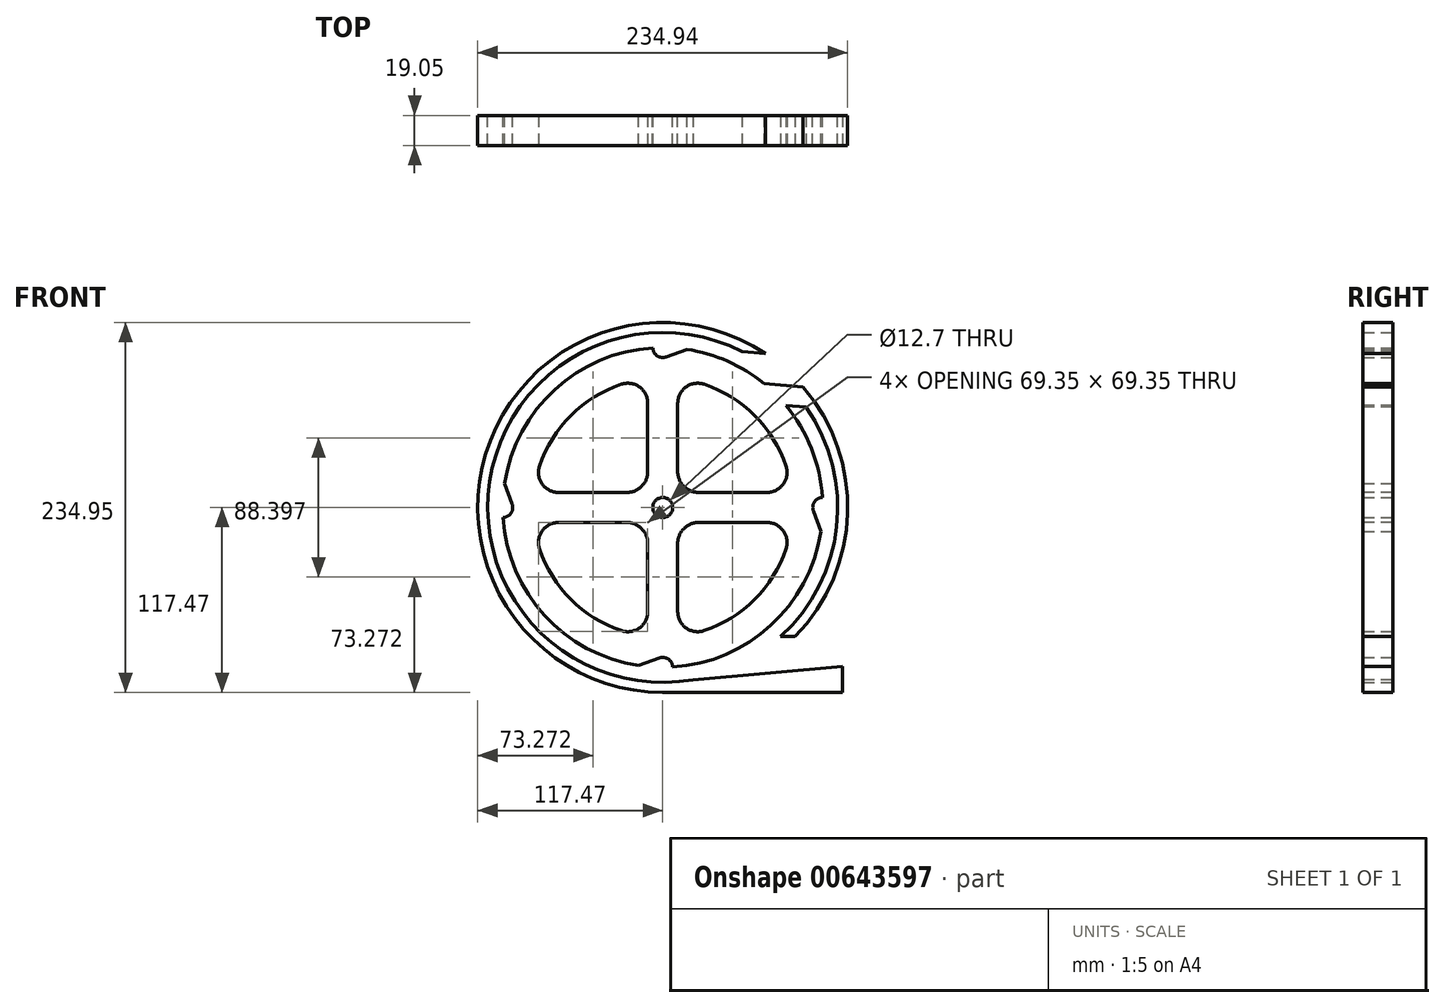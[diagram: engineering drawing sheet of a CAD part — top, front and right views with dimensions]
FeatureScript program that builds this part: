
annotation { "Feature Type Name" : "Feature", "Feature Type Description" : "" }
export const myFeature = defineFeature(function(context is Context, id is Id, definition is map)
    precondition{}
    {
        {
            var Q0;
            Q0=qCreatedBy(makeId("Front.planeOp"),FACE);
            var sketch = newSketch(context, id + "F0", { "sketchPlane" : qUnion([Q0])});
            skArc(sketch, "E0", {"start": v(-6.35, 101.4) * mm, "mid": v(-68.57, 74.97) * mm, "end": v(-100.43, 15.36) * mm});
            skArc(sketch, "E1", {"start": v(-6.35, 101.4) * mm, "mid": v(-3.56, 96.34) * mm, "end": v(2.17, 95.63) * mm});
            skLineSegment(sketch, "E2", {"start": v(0, 101.6) * mm, "end": v(18.57, 101.6) * mm, "construction": true});
            skLineSegment(sketch, "E3", {"start": v(15.36, 100.43) * mm, "end": v(2.17, 95.63) * mm});
            skLineSegment(sketch, "E4", {"start": v(15.36, 100.43) * mm, "end": v(18.57, 101.6) * mm, "construction": true});
            skLineSegment(sketch, "E5.1.0", {"start": v(-100.43, 15.36) * mm, "end": v(-95.63, 2.17) * mm});
            skArc(sketch, "E5.1.1", {"start": v(-101.4, -6.35) * mm, "mid": v(-96.34, -3.56) * mm, "end": v(-95.63, 2.17) * mm});
            skLineSegment(sketch, "E5.2.0", {"start": v(-15.36, -100.43) * mm, "end": v(-2.17, -95.63) * mm});
            skArc(sketch, "E5.2.1", {"start": v(6.35, -101.4) * mm, "mid": v(3.56, -96.34) * mm, "end": v(-2.17, -95.63) * mm});
            skLineSegment(sketch, "E5.3.0", {"start": v(100.43, -15.36) * mm, "end": v(95.63, -2.17) * mm});
            skArc(sketch, "E5.3.1", {"start": v(101.4, 6.35) * mm, "mid": v(96.34, 3.56) * mm, "end": v(95.63, -2.17) * mm});
            skArc(sketch, "E6.trimOffspring", {"start": v(-101.4, -6.35) * mm, "mid": v(-74.97, -68.57) * mm, "end": v(-15.36, -100.43) * mm});
            skArc(sketch, "E7.trimOffspring", {"start": v(101.4, 6.35) * mm, "mid": v(74.97, 68.57) * mm, "end": v(15.36, 100.43) * mm});
            skArc(sketch, "E8.trimOffspring", {"start": v(6.35, -101.4) * mm, "mid": v(68.57, -74.97) * mm, "end": v(100.43, -15.36) * mm});
            skCircle(sketch, "E9", {"center": v(0, 0) * mm, "radius": 6.35 * mm});
            skSolve(sketch);
        }
        {
            var Q0;
            Q0=makeQuery(id+"F0.imprint","IMPRINT",FACE,{"disambiguationData":[TD([[makeQuery(id+"F0.imprint","IMPRINT",EDGE,{"derivedFrom":sQuery(id+"F0.wireOp",EDGE,"E0")}),1.0]])]});
            extrude(context, id + "F1", {"entities" : qUnion([Q0]), "depth" : 19.05 * mm, "offsetDistance" : 25.4 * mm});
        }
        {
            var Q0;
            Q0=makeQuery(id+"F1.opExtrude","CAP_FACE",FACE,{"disambiguationData":[OSD([sQuery(id+"F0.wireOp",EDGE,"E0"),sQuery(id+"F0.wireOp",EDGE,"E1"),sQuery(id+"F0.wireOp",EDGE,"E3"),sQuery(id+"F0.wireOp",EDGE,"E5.1.0"),sQuery(id+"F0.wireOp",EDGE,"E5.1.1"),sQuery(id+"F0.wireOp",EDGE,"E5.2.0"),sQuery(id+"F0.wireOp",EDGE,"E5.2.1"),sQuery(id+"F0.wireOp",EDGE,"E5.3.0"),sQuery(id+"F0.wireOp",EDGE,"E5.3.1"),sQuery(id+"F0.wireOp",EDGE,"E6.trimOffspring"),sQuery(id+"F0.wireOp",EDGE,"E7.trimOffspring"),sQuery(id+"F0.wireOp",EDGE,"E8.trimOffspring"),sQuery(id+"F0.wireOp",EDGE,"E9")])],"isStart":false});
            var sketch = newSketch(context, id + "F2", { "sketchPlane" : qUnion([Q0])});
            skCircle(sketch, "E10", {"center": v(0, 0) * mm, "radius": 19.05 * mm});
            skCircle(sketch, "E11", {"center": v(0, 0) * mm, "radius": 82.55 * mm});
            skLineSegment(sketch, "E12", {"start": v(9.53, 16.5) * mm, "end": v(9.53, 82) * mm});
            skLineSegment(sketch, "E13", {"start": v(-9.53, 16.5) * mm, "end": v(-9.53, 82) * mm});
            skLineSegment(sketch, "E14", {"start": v(0, 0) * mm, "end": v(0, 82.55) * mm, "construction": true});
            skLineSegment(sketch, "E15.1.0", {"start": v(-16.5, 9.53) * mm, "end": v(-82, 9.52) * mm});
            skLineSegment(sketch, "E15.1.1", {"start": v(-16.5, -9.52) * mm, "end": v(-82, -9.53) * mm});
            skLineSegment(sketch, "E15.2.0", {"start": v(-9.53, -16.5) * mm, "end": v(-9.52, -82) * mm});
            skLineSegment(sketch, "E15.2.1", {"start": v(9.52, -16.5) * mm, "end": v(9.53, -82) * mm});
            skLineSegment(sketch, "E15.3.0", {"start": v(16.5, -9.53) * mm, "end": v(82, -9.52) * mm});
            skLineSegment(sketch, "E15.3.1", {"start": v(16.5, 9.52) * mm, "end": v(82, 9.53) * mm});
            skSolve(sketch);
        }
        {
            var Q0;
            {var subQ0=sQuery(id+"F2.wireOp",EDGE,"E12");Q0=makeQuery(id+"F2.imprint","IMPRINT",FACE,{"disambiguationData":[TD([[makeQuery(id+"F2.imprint","IMPRINT",EDGE,{"derivedFrom":subQ0}),-1.0]])]});}
            var Q1;
            {var subQ0=sQuery(id+"F2.wireOp",EDGE,"E13");Q1=makeQuery(id+"F2.imprint","IMPRINT",FACE,{"disambiguationData":[TD([[makeQuery(id+"F2.imprint","IMPRINT",EDGE,{"derivedFrom":subQ0}),1.0]])]});}
            var Q2;
            {var subQ0=sQuery(id+"F2.wireOp",EDGE,"E15.1.1");Q2=makeQuery(id+"F2.imprint","IMPRINT",FACE,{"disambiguationData":[TD([[makeQuery(id+"F2.imprint","IMPRINT",EDGE,{"derivedFrom":subQ0}),1.0]])]});}
            var Q3;
            {var subQ0=sQuery(id+"F2.wireOp",EDGE,"E15.2.1");Q3=makeQuery(id+"F2.imprint","IMPRINT",FACE,{"disambiguationData":[TD([[makeQuery(id+"F2.imprint","IMPRINT",EDGE,{"derivedFrom":subQ0}),1.0]])]});}
            var Q4;
            {var subQ0=sQuery(id+"F2.wireOp",EDGE,"E15.3.1");Q4=makeQuery(id+"F2.imprint","IMPRINT",FACE,{"disambiguationData":[TD([[makeQuery(id+"F2.imprint","IMPRINT",EDGE,{"derivedFrom":subQ0}),1.0]])]});}
            extrude(context, id + "F3", {"entities" : qUnion([Q0, Q1, Q2, Q3, Q4]), "operationType" : NewBodyOperationType.REMOVE, "oppositeDirection" : true, "depth" : 19.05 * mm, "offsetDistance" : 25.4 * mm});
        }
        {
            var Q0;
            Q0=makeQuery(id+"F3.boolean.opBoolean","COPY",EDGE,{"derivedFrom":makeQuery(id+"F3.opExtrude","SWEPT_EDGE",EDGE,{"disambiguationData":[OSD([sQuery(id+"F2.wireOp",EDGE,"E11"),sQuery(id+"F2.wireOp",EDGE,"E13")])]})});
            var Q1;
            Q1=makeQuery(id+"F3.boolean.opBoolean","COPY",EDGE,{"derivedFrom":makeQuery(id+"F3.opExtrude","SWEPT_EDGE",EDGE,{"disambiguationData":[OSD([sQuery(id+"F2.wireOp",EDGE,"E11"),sQuery(id+"F2.wireOp",EDGE,"E15.1.0")])]})});
            var Q2;
            Q2=makeQuery(id+"F3.boolean.opBoolean","COPY",EDGE,{"derivedFrom":makeQuery(id+"F3.opExtrude","SWEPT_EDGE",EDGE,{"disambiguationData":[OSD([sQuery(id+"F2.wireOp",EDGE,"E10"),sQuery(id+"F2.wireOp",EDGE,"E13")])]})});
            var Q3;
            Q3=makeQuery(id+"F3.boolean.opBoolean","COPY",EDGE,{"derivedFrom":makeQuery(id+"F3.opExtrude","SWEPT_EDGE",EDGE,{"disambiguationData":[OSD([sQuery(id+"F2.wireOp",EDGE,"E10"),sQuery(id+"F2.wireOp",EDGE,"E15.1.0")])]})});
            var Q4;
            Q4=makeQuery(id+"F3.boolean.opBoolean","COPY",EDGE,{"derivedFrom":makeQuery(id+"F3.opExtrude","SWEPT_EDGE",EDGE,{"disambiguationData":[OSD([sQuery(id+"F2.wireOp",EDGE,"E11"),sQuery(id+"F2.wireOp",EDGE,"c7ea23de-dd5f-4fa7-8742-d0bc3a6b1323.3.4.0")])]})});
            var Q5;
            Q5=makeQuery(id+"F3.boolean.opBoolean","COPY",EDGE,{"derivedFrom":makeQuery(id+"F3.opExtrude","SWEPT_EDGE",EDGE,{"disambiguationData":[OSD([sQuery(id+"F2.wireOp",EDGE,"E11"),sQuery(id+"F2.wireOp",EDGE,"E12")])]})});
            var Q6;
            Q6=makeQuery(id+"F3.boolean.opBoolean","COPY",EDGE,{"derivedFrom":makeQuery(id+"F3.opExtrude","SWEPT_EDGE",EDGE,{"disambiguationData":[OSD([sQuery(id+"F2.wireOp",EDGE,"E10"),sQuery(id+"F2.wireOp",EDGE,"E12")])]})});
            var Q7;
            Q7=makeQuery(id+"F3.boolean.opBoolean","COPY",EDGE,{"derivedFrom":makeQuery(id+"F3.opExtrude","SWEPT_EDGE",EDGE,{"disambiguationData":[OSD([sQuery(id+"F2.wireOp",EDGE,"E10"),sQuery(id+"F2.wireOp",EDGE,"c7ea23de-dd5f-4fa7-8742-d0bc3a6b1323.3.4.0")])]})});
            var Q8;
            Q8=makeQuery(id+"F3.boolean.opBoolean","COPY",EDGE,{"derivedFrom":makeQuery(id+"F3.opExtrude","SWEPT_EDGE",EDGE,{"disambiguationData":[OSD([sQuery(id+"F2.wireOp",EDGE,"E10"),sQuery(id+"F2.wireOp",EDGE,"E15.3.1")])]})});
            var Q9;
            Q9=makeQuery(id+"F3.boolean.opBoolean","COPY",EDGE,{"derivedFrom":makeQuery(id+"F3.opExtrude","SWEPT_EDGE",EDGE,{"disambiguationData":[OSD([sQuery(id+"F2.wireOp",EDGE,"E11"),sQuery(id+"F2.wireOp",EDGE,"E15.3.1")])]})});
            var Q10;
            Q10=makeQuery(id+"F3.boolean.opBoolean","COPY",EDGE,{"derivedFrom":makeQuery(id+"F3.opExtrude","SWEPT_EDGE",EDGE,{"disambiguationData":[OSD([sQuery(id+"F2.wireOp",EDGE,"E11"),sQuery(id+"F2.wireOp",EDGE,"c7ea23de-dd5f-4fa7-8742-d0bc3a6b1323.1.4.0")])]})});
            var Q11;
            Q11=makeQuery(id+"F3.boolean.opBoolean","COPY",EDGE,{"derivedFrom":makeQuery(id+"F3.opExtrude","SWEPT_EDGE",EDGE,{"disambiguationData":[OSD([sQuery(id+"F2.wireOp",EDGE,"E10"),sQuery(id+"F2.wireOp",EDGE,"c7ea23de-dd5f-4fa7-8742-d0bc3a6b1323.1.4.0")])]})});
            var Q12;
            Q12=makeQuery(id+"F3.boolean.opBoolean","COPY",EDGE,{"derivedFrom":makeQuery(id+"F3.opExtrude","SWEPT_EDGE",EDGE,{"disambiguationData":[OSD([sQuery(id+"F2.wireOp",EDGE,"E10"),sQuery(id+"F2.wireOp",EDGE,"E15.3.0")])]})});
            var Q13;
            Q13=makeQuery(id+"F3.boolean.opBoolean","COPY",EDGE,{"derivedFrom":makeQuery(id+"F3.opExtrude","SWEPT_EDGE",EDGE,{"disambiguationData":[OSD([sQuery(id+"F2.wireOp",EDGE,"E11"),sQuery(id+"F2.wireOp",EDGE,"E15.3.0")])]})});
            var Q14;
            Q14=makeQuery(id+"F3.boolean.opBoolean","COPY",EDGE,{"derivedFrom":makeQuery(id+"F3.opExtrude","SWEPT_EDGE",EDGE,{"disambiguationData":[OSD([sQuery(id+"F2.wireOp",EDGE,"E11"),sQuery(id+"F2.wireOp",EDGE,"E15.2.1")])]})});
            var Q15;
            Q15=makeQuery(id+"F3.boolean.opBoolean","COPY",EDGE,{"derivedFrom":makeQuery(id+"F3.opExtrude","SWEPT_EDGE",EDGE,{"disambiguationData":[OSD([sQuery(id+"F2.wireOp",EDGE,"E10"),sQuery(id+"F2.wireOp",EDGE,"E15.2.1")])]})});
            var Q16;
            Q16=makeQuery(id+"F3.boolean.opBoolean","COPY",EDGE,{"derivedFrom":makeQuery(id+"F3.opExtrude","SWEPT_EDGE",EDGE,{"disambiguationData":[OSD([sQuery(id+"F2.wireOp",EDGE,"E10"),sQuery(id+"F2.wireOp",EDGE,"E15.2.0")])]})});
            var Q17;
            Q17=makeQuery(id+"F3.boolean.opBoolean","COPY",EDGE,{"derivedFrom":makeQuery(id+"F3.opExtrude","SWEPT_EDGE",EDGE,{"disambiguationData":[OSD([sQuery(id+"F2.wireOp",EDGE,"E10"),sQuery(id+"F2.wireOp",EDGE,"E15.1.1")])]})});
            var Q18;
            Q18=makeQuery(id+"F3.boolean.opBoolean","COPY",EDGE,{"derivedFrom":makeQuery(id+"F3.opExtrude","SWEPT_EDGE",EDGE,{"disambiguationData":[OSD([sQuery(id+"F2.wireOp",EDGE,"E11"),sQuery(id+"F2.wireOp",EDGE,"E15.1.1")])]})});
            var Q19;
            Q19=makeQuery(id+"F3.boolean.opBoolean","COPY",EDGE,{"derivedFrom":makeQuery(id+"F3.opExtrude","SWEPT_EDGE",EDGE,{"disambiguationData":[OSD([sQuery(id+"F2.wireOp",EDGE,"E11"),sQuery(id+"F2.wireOp",EDGE,"E15.2.0")])]})});
            fillet(context, id + "F4", {"entities" : qUnion([Q0, Q1, Q2, Q3, Q4, Q5, Q6, Q7, Q8, Q9, Q10, Q11, Q12, Q13, Q14, Q15, Q16, Q17, Q18, Q19]), "radius" : 12.7 * mm, "tangentPropagation" : true, "allowEdgeOverflow" : false});
        }
        {
            var Q0;
            Q0=qCreatedBy(makeId("Front.planeOp"),FACE);
            var sketch = newSketch(context, id + "F5", { "sketchPlane" : qUnion([Q0])});
            skCircle(sketch, "E16", {"center": v(0, 0) * mm, "radius": 111.13 * mm});
            skCircle(sketch, "E17", {"center": v(0, 0) * mm, "radius": 117.48 * mm});
            skSolve(sketch);
        }
        {
            var Q0;
            Q0=makeQuery(id+"F5.imprint","IMPRINT",FACE,{"disambiguationData":[TD([[makeQuery(id+"F5.imprint","IMPRINT",EDGE,{"derivedFrom":sQuery(id+"F5.wireOp",EDGE,"E16")}),-1.0]])]});
            extrude(context, id + "F6", {"entities" : qUnion([Q0]), "depth" : 19.05 * mm, "offsetDistance" : 25.4 * mm});
        }
        {
            var Q0;
            Q0=makeQuery(id+"F6.opExtrude","CAP_FACE",FACE,{"disambiguationData":[OSD([sQuery(id+"F5.wireOp",EDGE,"E16"),sQuery(id+"F5.wireOp",EDGE,"E17")])],"isStart":false});
            var sketch = newSketch(context, id + "F7", { "sketchPlane" : qUnion([Q0])});
            skLineSegment(sketch, "E18", {"start": v(0, -111.13) * mm, "end": v(114.3, -101.13) * mm});
            skLineSegment(sketch, "E19", {"start": v(114.3, -101.13) * mm, "end": v(114.3, -117.47) * mm});
            skLineSegment(sketch, "E20", {"start": v(114.3, -117.47) * mm, "end": v(0, -117.47) * mm});
            skLineSegment(sketch, "E21", {"start": v(0, -117.47) * mm, "end": v(0, -111.13) * mm});
            skLineSegment(sketch, "E22", {"start": v(114.3, -101.13) * mm, "end": v(114.3, -82.08) * mm});
            skLineSegment(sketch, "E23", {"start": v(114.3, -82.08) * mm, "end": v(84.05, -82.08) * mm});
            skLineSegment(sketch, "E24", {"start": v(84.05, -82.08) * mm, "end": v(74.92, -82.08) * mm});
            skLineSegment(sketch, "E25", {"start": v(74.92, -82.08) * mm, "end": v(0, -111.12) * mm});
            skSolve(sketch);
        }
        {
            var Q0;
            {var subQ0=sQuery(id+"F7.wireOp",EDGE,"E19");Q0=makeQuery(id+"F7.imprint","IMPRINT",FACE,{"disambiguationData":[TD([[makeQuery(id+"F7.imprint","IMPRINT",EDGE,{"derivedFrom":subQ0}),-1.0]])]});}
            extrude(context, id + "F8", {"entities" : qUnion([Q0]), "operationType" : NewBodyOperationType.ADD, "oppositeDirection" : true, "depth" : 19.05 * mm, "offsetDistance" : 25.4 * mm});
        }
        {
            var Q0;
            {var subQ5=sQuery(id+"F7.wireOp",EDGE,"E24");Q0=makeQuery(id+"F7.imprint","IMPRINT",FACE,{"disambiguationData":[TD([[makeQuery(id+"F7.imprint","IMPRINT",EDGE,{"derivedFrom":subQ5}),1.0]])]});}
            extrude(context, id + "F9", {"entities" : qUnion([Q0]), "operationType" : NewBodyOperationType.REMOVE, "oppositeDirection" : true, "depth" : 19.05 * mm, "offsetDistance" : 25.4 * mm});
        }
        {
            var Q0;
            Q0=makeQuery(id+"F1.opExtrude","CAP_FACE",FACE,{"disambiguationData":[OSD([sQuery(id+"F0.wireOp",EDGE,"E0"),sQuery(id+"F0.wireOp",EDGE,"E1"),sQuery(id+"F0.wireOp",EDGE,"E3"),sQuery(id+"F0.wireOp",EDGE,"E5.1.0"),sQuery(id+"F0.wireOp",EDGE,"E5.1.1"),sQuery(id+"F0.wireOp",EDGE,"E5.2.0"),sQuery(id+"F0.wireOp",EDGE,"E5.2.1"),sQuery(id+"F0.wireOp",EDGE,"E5.3.0"),sQuery(id+"F0.wireOp",EDGE,"E5.3.1"),sQuery(id+"F0.wireOp",EDGE,"E6.trimOffspring"),sQuery(id+"F0.wireOp",EDGE,"E7.trimOffspring"),sQuery(id+"F0.wireOp",EDGE,"E8.trimOffspring"),sQuery(id+"F0.wireOp",EDGE,"E9")])],"isStart":false});
            var sketch = newSketch(context, id + "F10", { "sketchPlane" : qUnion([Q0])});
            skPoint(sketch, "E26.0", {"position": v(0, 101.6) * mm});
            skCircle(sketch, "E27", {"center": v(0, 101.6) * mm, "radius": 6.35 * mm});
            skLineSegment(sketch, "E28.0", {"start": v(15.36, 100.43) * mm, "end": v(2.17, 95.63) * mm, "construction": true});
            skLineSegment(sketch, "E29.0.2", {"start": v(47.45, 80.22) * mm, "end": v(64.18, 78.76) * mm, "construction": true});
            skArc(sketch, "E30.0", {"start": v(84.05, -82.08) * mm, "mid": v(-45.6, 108.26) * mm, "end": v(0, -117.47) * mm, "construction": true});
            skLineSegment(sketch, "E31", {"start": v(64.18, 78.76) * mm, "end": v(89.08, 76.58) * mm});
            skLineSegment(sketch, "E32", {"start": v(89.08, 76.58) * mm, "end": v(89.08, 95.63) * mm});
            skLineSegment(sketch, "E33", {"start": v(64.18, 78.76) * mm, "end": v(67.34, 78.48) * mm});
            skLineSegment(sketch, "E34.0", {"start": v(60.33, 66.35) * mm, "end": v(91.08, 63.66) * mm});
            skLineSegment(sketch, "E35", {"start": v(67.34, 78.48) * mm, "end": v(81.44, 64.5) * mm});
            skPoint(sketch, "E36", {"position": v(78.27, 64.78) * mm});
            skLineSegment(sketch, "E37", {"start": v(89.08, 76.58) * mm, "end": v(91.08, 63.66) * mm});
            skLineSegment(sketch, "E38", {"start": v(89.08, 95.63) * mm, "end": v(50.45, 99.01) * mm});
            skLineSegment(sketch, "E39", {"start": v(50.45, 99.01) * mm, "end": v(64.18, 78.76) * mm});
            skSolve(sketch);
        }
        {
            var Q0;
            Q0=makeQuery(id+"F10.imprint","IMPRINT",FACE,{"disambiguationData":[TD([[makeQuery(id+"F10.imprint","IMPRINT",EDGE,{"derivedFrom":sQuery(id+"F10.wireOp",EDGE,"E31")}),-1.0]])]});
            extrude(context, id + "F11", {"entities" : qUnion([Q0]), "operationType" : NewBodyOperationType.ADD, "oppositeDirection" : true, "depth" : 19.05 * mm, "offsetDistance" : 25.4 * mm});
        }
        {
            var Q0;
            {var subQ2=sQuery(id+"F10.wireOp",EDGE,"E31");Q0=makeQuery(id+"F10.imprint","IMPRINT",FACE,{"disambiguationData":[TD([[makeQuery(id+"F10.imprint","IMPRINT",EDGE,{"derivedFrom":subQ2}),1.0]])]});}
            extrude(context, id + "F12", {"entities" : qUnion([Q0]), "operationType" : NewBodyOperationType.REMOVE, "oppositeDirection" : true, "depth" : 25.4 * mm, "offsetDistance" : 25.4 * mm});
        }
    });
